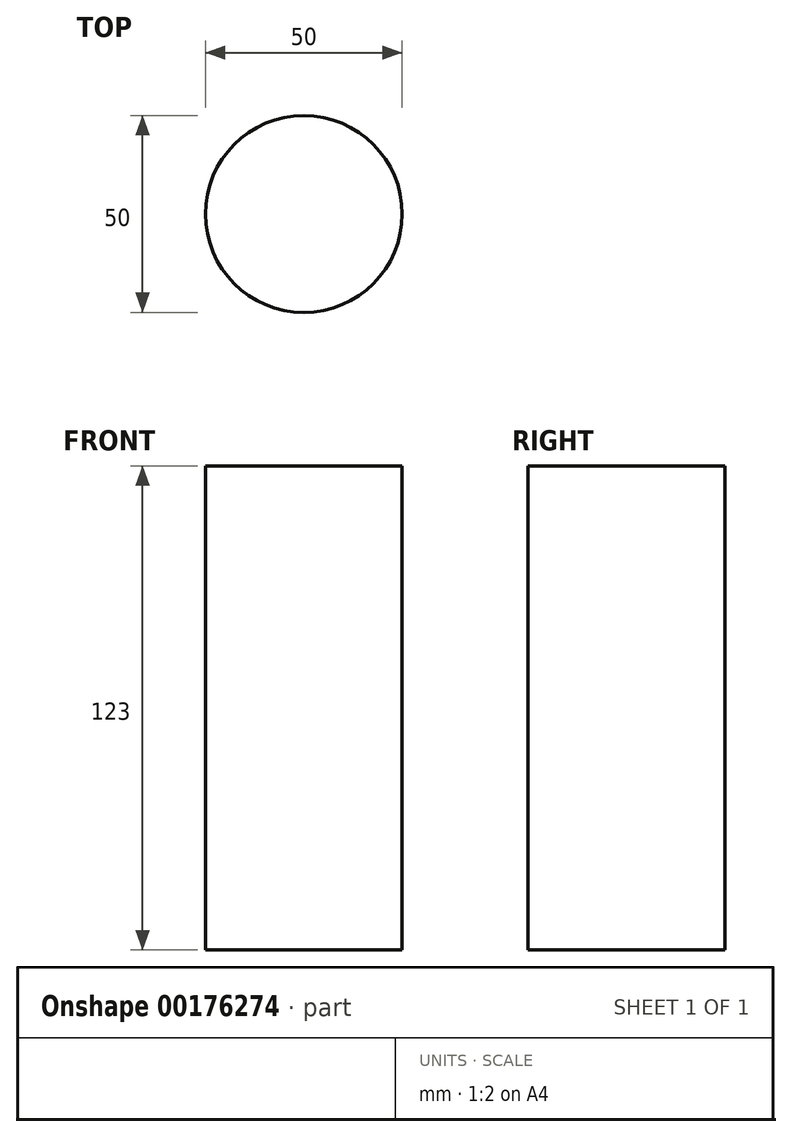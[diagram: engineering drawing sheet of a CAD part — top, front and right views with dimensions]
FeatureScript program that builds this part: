
annotation { "Feature Type Name" : "Feature", "Feature Type Description" : "" }
export const myFeature = defineFeature(function(context is Context, id is Id, definition is map)
    precondition{}
    {
        {
            var Q0;
            Q0=qCreatedBy(makeId("Top.planeOp"),FACE);
            var sketch = newSketch(context, id + "F0", { "sketchPlane" : qUnion([Q0])});
            skCircle(sketch, "E0", {"center": v(0, 0) * mm, "radius": 25 * mm});
            skSolve(sketch);
        }
        {
            var Q0;
            Q0 = qSketchRegion(id + "F0", true);
            extrude(context, id + "F1", {"entities" : qUnion([Q0]), "depth" : 123 * mm});
        }
    });
